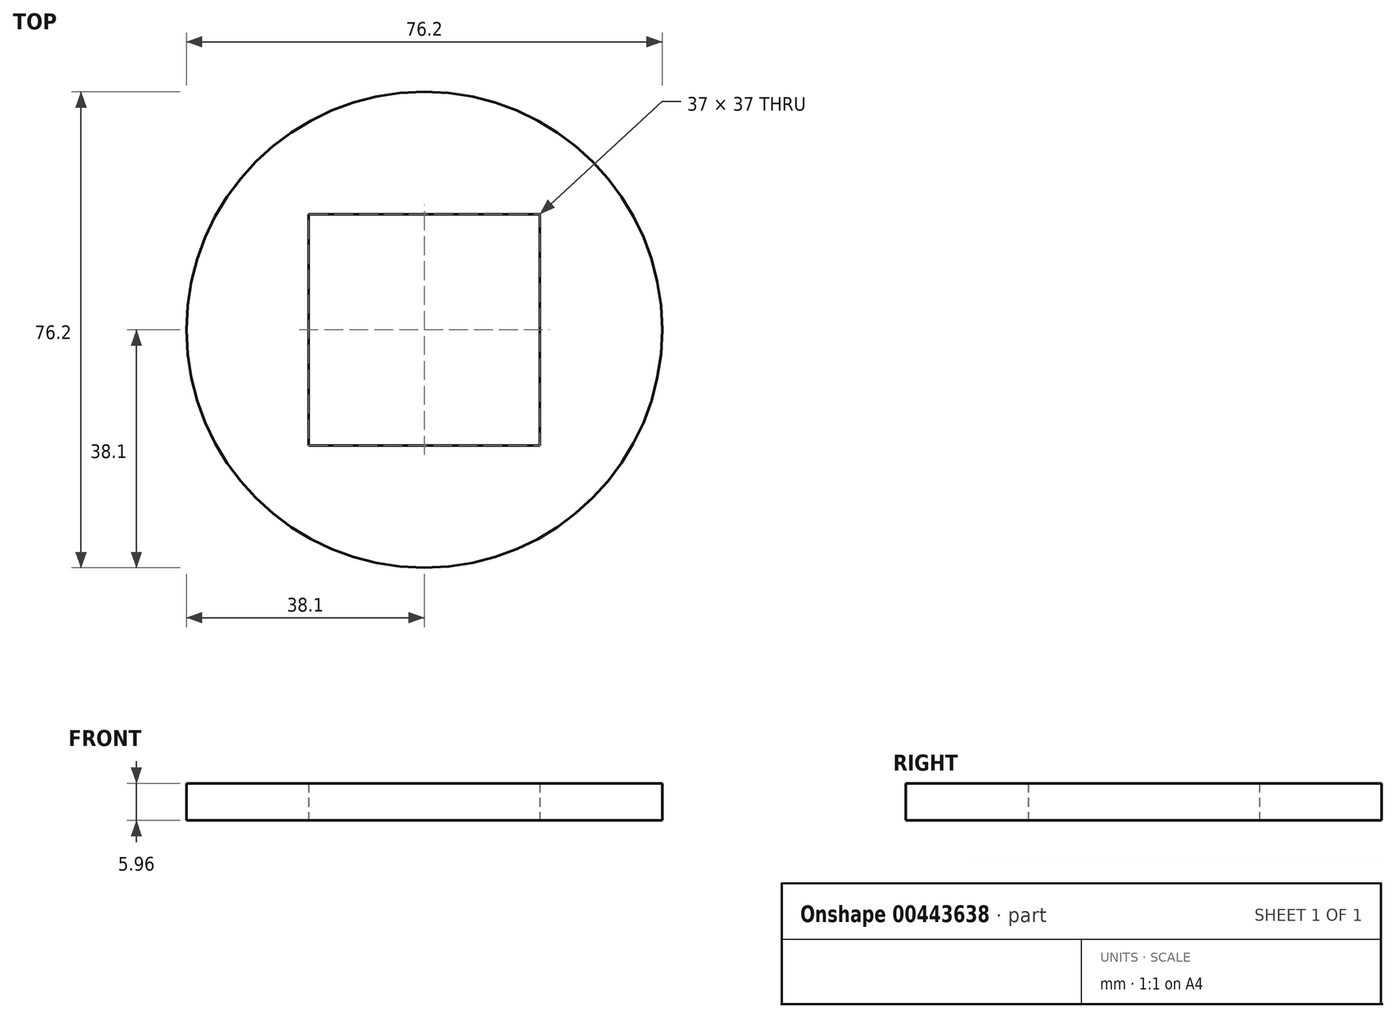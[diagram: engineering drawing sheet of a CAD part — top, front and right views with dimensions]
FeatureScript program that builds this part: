
annotation { "Feature Type Name" : "Feature", "Feature Type Description" : "" }
export const myFeature = defineFeature(function(context is Context, id is Id, definition is map)
    precondition{}
    {
        {
            var Q0;
            Q0=qCreatedBy(makeId("Top.planeOp"),FACE);
            var sketch = newSketch(context, id + "F0", { "sketchPlane" : qUnion([Q0])});
            skCircle(sketch, "E0", {"center": v(0, 0) * mm, "radius": 38.1 * mm});
            skLineSegment(sketch, "E1.bottom", {"start": v(18.5, 18.5) * mm, "end": v(-18.5, 18.5) * mm});
            skLineSegment(sketch, "E1.top", {"start": v(18.5, -18.5) * mm, "end": v(-18.5, -18.5) * mm});
            skLineSegment(sketch, "E1.left", {"start": v(18.5, 18.5) * mm, "end": v(18.5, -18.5) * mm});
            skLineSegment(sketch, "E1.right", {"start": v(-18.5, 18.5) * mm, "end": v(-18.5, -18.5) * mm});
            skSolve(sketch);
        }
        {
            var Q0;
            Q0=makeQuery(id+"F0.imprint","IMPRINT",FACE,{"disambiguationData":[TD([[makeQuery(id+"F0.imprint","IMPRINT",EDGE,{"derivedFrom":sQuery(id+"F0.wireOp",EDGE,"E0")}),1.0]])]});
            extrude(context, id + "F1", {"entities" : qUnion([Q0]), "depth" : 5.96 * mm});
        }
    });
